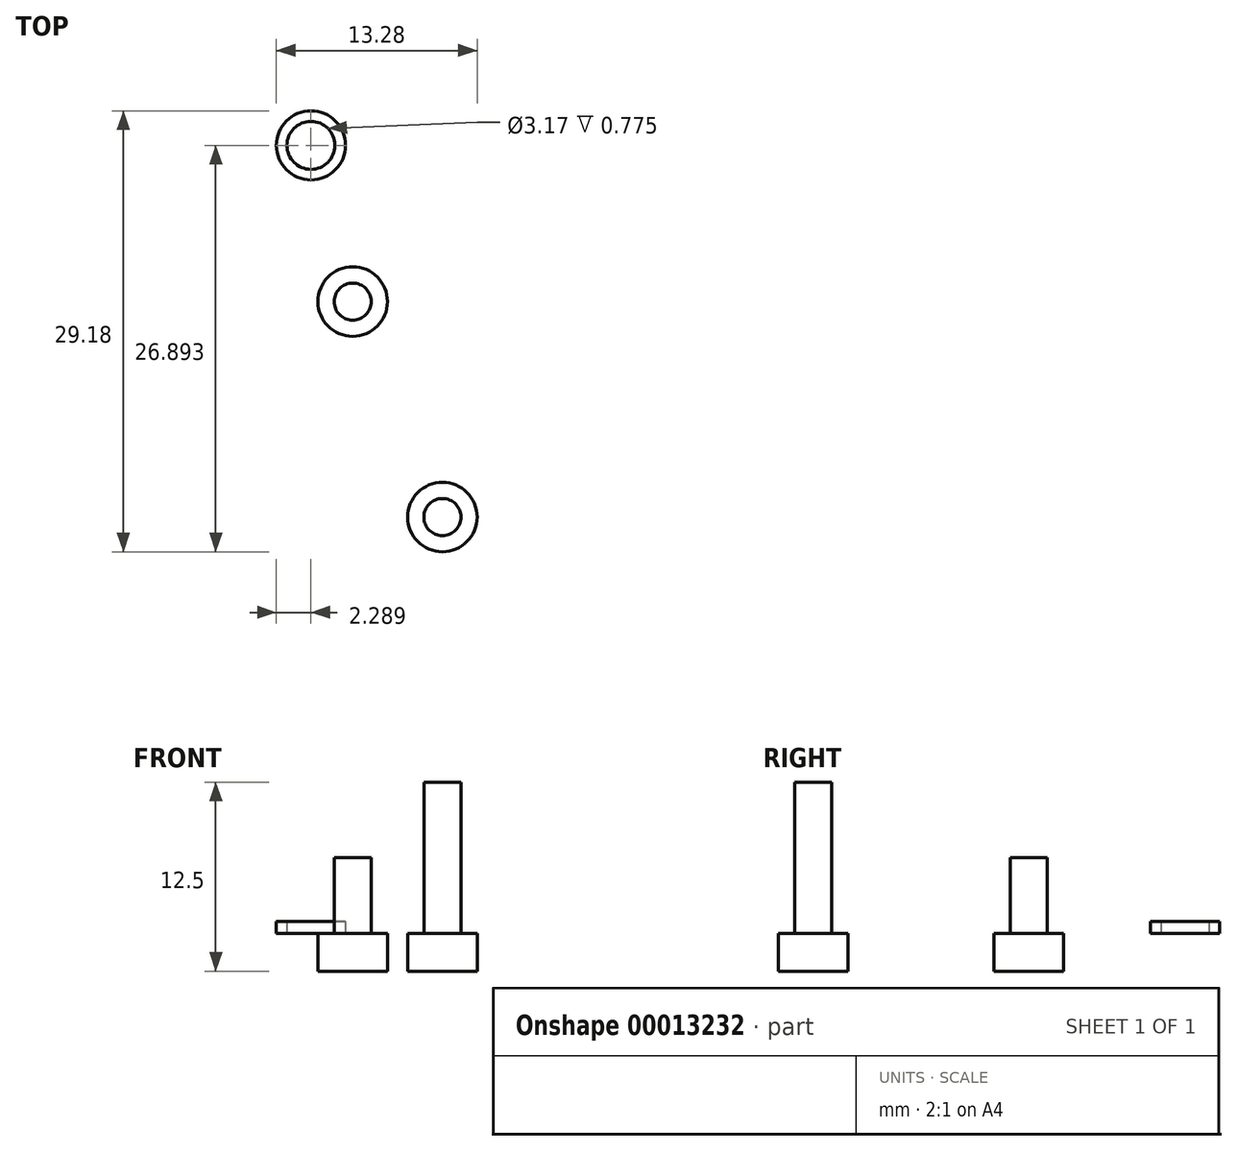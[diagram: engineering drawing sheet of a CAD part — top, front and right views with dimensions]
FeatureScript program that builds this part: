
annotation { "Feature Type Name" : "Feature", "Feature Type Description" : "" }
export const myFeature = defineFeature(function(context is Context, id is Id, definition is map)
    precondition{}
    {
        {
            var Q0;
            Q0=qCreatedBy(makeId("Top.planeOp"),FACE);
            var sketch = newSketch(context, id + "F0", { "sketchPlane" : qUnion([Q0])});
            skCircle(sketch, "E0", {"center": v(-46.53, 43.86) * mm, "radius": 1.59 * mm});
            skCircle(sketch, "E1", {"center": v(-46.53, 43.86) * mm, "radius": 2.29 * mm});
            skSolve(sketch);
        }
        {
            var Q0;
            Q0=makeQuery(id+"F0.imprint","IMPRINT",FACE,{"disambiguationData":[TD([[makeQuery(id+"F0.imprint","IMPRINT",EDGE,{"derivedFrom":sQuery(id+"F0.wireOp",EDGE,"E0")}),-1.0]])]});
            extrude(context, id + "F1", {"entities" : qUnion([Q0]), "depth" : 0.77 * mm});
        }
        {
            var Q0;
            Q0=qCreatedBy(makeId("Top.planeOp"),FACE);
            var sketch = newSketch(context, id + "F2", { "sketchPlane" : qUnion([Q0])});
            skCircle(sketch, "E2", {"center": v(-37.84, 19.27) * mm, "radius": 2.3 * mm});
            skCircle(sketch, "E3", {"center": v(-37.84, 19.27) * mm, "radius": 1.23 * mm});
            skSolve(sketch);
        }
        {
            var Q0;
            Q0=makeQuery(id+"F2.imprint","IMPRINT",FACE,{"disambiguationData":[TD([[makeQuery(id+"F2.imprint","IMPRINT",EDGE,{"derivedFrom":sQuery(id+"F2.wireOp",EDGE,"E2")}),1.0]])]});
            var Q1;
            Q1=makeQuery(id+"F2.imprint","IMPRINT",FACE,{"disambiguationData":[TD([[makeQuery(id+"F2.imprint","IMPRINT",EDGE,{"derivedFrom":sQuery(id+"F2.wireOp",EDGE,"E3")}),1.0]])]});
            extrude(context, id + "F3", {"entities" : qUnion([Q0, Q1]), "oppositeDirection" : true, "depth" : 2.5 * mm});
        }
        {
            var Q0;
            Q0=makeQuery(id+"F2.imprint","IMPRINT",FACE,{"disambiguationData":[TD([[makeQuery(id+"F2.imprint","IMPRINT",EDGE,{"derivedFrom":sQuery(id+"F2.wireOp",EDGE,"E3")}),1.0]])]});
            extrude(context, id + "F4", {"entities" : qUnion([Q0]), "operationType" : NewBodyOperationType.ADD, "depth" : 10 * mm});
        }
        {
            var Q0;
            Q0=qCreatedBy(makeId("Top.planeOp"),FACE);
            var sketch = newSketch(context, id + "F5", { "sketchPlane" : qUnion([Q0])});
            skCircle(sketch, "E4", {"center": v(-43.77, 33.53) * mm, "radius": 2.3 * mm});
            skCircle(sketch, "E5", {"center": v(-43.77, 33.53) * mm, "radius": 1.23 * mm});
            skSolve(sketch);
        }
        {
            var Q0;
            Q0=makeQuery(id+"F5.imprint","IMPRINT",FACE,{"disambiguationData":[TD([[makeQuery(id+"F5.imprint","IMPRINT",EDGE,{"derivedFrom":sQuery(id+"F5.wireOp",EDGE,"E5")}),1.0]])]});
            var Q1;
            Q1=makeQuery(id+"F5.imprint","IMPRINT",FACE,{"disambiguationData":[TD([[makeQuery(id+"F5.imprint","IMPRINT",EDGE,{"derivedFrom":sQuery(id+"F5.wireOp",EDGE,"E4")}),1.0]])]});
            extrude(context, id + "F6", {"entities" : qUnion([Q0, Q1]), "oppositeDirection" : true, "depth" : 2.5 * mm});
        }
        {
            var Q0;
            Q0=makeQuery(id+"F5.imprint","IMPRINT",FACE,{"disambiguationData":[TD([[makeQuery(id+"F5.imprint","IMPRINT",EDGE,{"derivedFrom":sQuery(id+"F5.wireOp",EDGE,"E5")}),1.0]])]});
            extrude(context, id + "F7", {"entities" : qUnion([Q0]), "operationType" : NewBodyOperationType.ADD, "depth" : 5 * mm});
        }
    });
